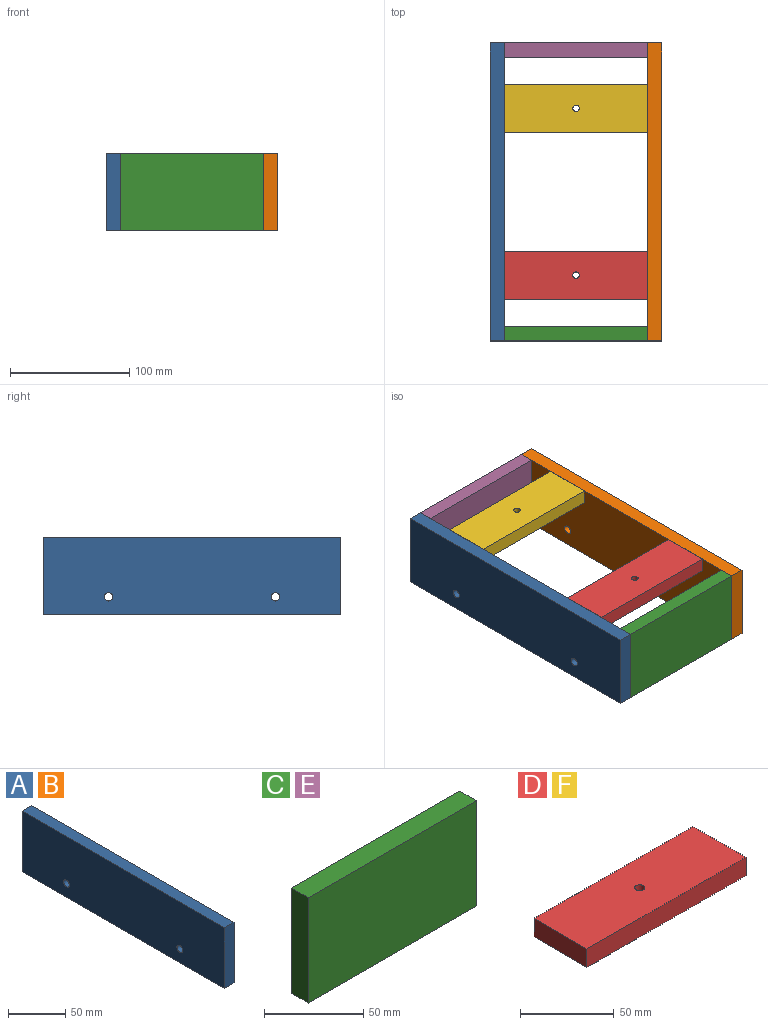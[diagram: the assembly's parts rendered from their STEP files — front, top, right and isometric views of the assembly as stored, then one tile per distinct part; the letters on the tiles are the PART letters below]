
ASSEMBLY  parts=6 mates=5
PART A: 8 faces, bbox 12x250x65 mm
  f0: plane 250x12mm, normal (0,0,1), area 3000mm2, adj f1,f3,f4,f5
  f1: plane 65x12mm, normal (0,-1,0), area 780mm2, adj f0,f2,f4,f5
  f2: plane 250x12mm, normal (0,0,-1), area 3000mm2, adj f1,f3,f4,f5
  f3: plane 65x12mm, normal (0,1,0), area 780mm2, adj f0,f2,f4,f5
  f4: plane 250x65mm, normal (1,0,0), area 16173mm2, adj f0,f1,f2,f3,f6,f7
  f5: plane 250x65mm, normal (-1,0,0), area 16173mm2, adj f0,f1,f2,f3,f6,f7
  f6: cylinder r=3.5mm len=12mm, axis (1,0,0), area 263.9mm2, adj f4,f5
  f7: cylinder r=3.5mm len=12mm, axis (1,0,0), area 263.9mm2, adj f4,f5
PART B: same geometry as A
PART C: 6 faces, bbox 120x12x65 mm
  f0: plane 120x12mm, normal (0,0,-1), area 1440mm2, adj f1,f3,f4,f5
  f1: plane 65x12mm, normal (1,0,0), area 780mm2, adj f0,f2,f4,f5
  f2: plane 120x12mm, normal (0,0,1), area 1440mm2, adj f1,f3,f4,f5
  f3: plane 65x12mm, normal (-1,0,0), area 780mm2, adj f0,f2,f4,f5
  f4: plane 120x65mm, normal (0,-1,0), area 7800mm2, adj f0,f1,f2,f3
  f5: plane 120x65mm, normal (0,1,0), area 7800mm2, adj f0,f1,f2,f3
PART D: 7 faces, bbox 120x40x12 mm
  f0: plane 120x12mm, normal (0,1,0), area 1440mm2, adj f1,f3,f4,f5
  f1: plane 40x12mm, normal (-1,0,0), area 480mm2, adj f0,f2,f4,f5
  f2: plane 120x12mm, normal (0,-1,0), area 1440mm2, adj f1,f3,f4,f5
  f3: plane 40x12mm, normal (1,0,0), area 480mm2, adj f0,f2,f4,f5
  f4: plane 120x40mm, normal (0,0,1), area 4776.3mm2, adj f0,f1,f2,f3,f6
  f5: plane 120x40mm, normal (0,0,-1), area 4776.3mm2, adj f0,f1,f2,f3,f6
  f6: cylinder r=2.75mm len=12mm, axis (0,0,1), area 207mm2, adj f4,f5
PART E: same geometry as C
PART F: same geometry as D
PLACE A t=(75.07,14.12,-175.48)mm
PLACE B t=(207.07,14.12,-175.48)mm
PLACE C t=(147.07,-95.69,-185.46)mm
PLACE D t=(147.07,-41.63,-164.96)mm
PLACE E t=(147.07,142.31,-185.46)mm
PLACE F t=(147.07,98.37,-164.96)mm
MATE fastened F.f4 <-> E.f2  axis (0,0,1) through (207.07,107.31,-152.96)mm
MATE fastened B.f5 <-> C.f1  axis (-1,0,0) through (207.07,-107.69,-185.46)mm
MATE fastened D.f4 <-> C.f2  axis (0,0,1) through (207.07,-72.69,-152.96)mm
MATE fastened B.f5 <-> E.f1  axis (-1,0,0) through (207.07,142.31,-152.96)mm
MATE fastened A.f4 <-> E.f3  axis (1,0,0) through (87.07,142.31,-217.96)mm
